# Revit family: Ghent - Reliant Series - Display Collection
name_source: partatom
category: Furniture
units: mm (PartAtom-declared; Revit-internal decimal feet)

## family parameters
Always vertical = Yes
Cut with Voids When Loaded = No
OmniClass Number = 23.40.20.00
OmniClass Title = General Furniture and Specialties
Room Calculation Point = No
Shared = No
Work Plane-Based = No

## types (7) — shared parameters
12 Shelves = No
Manufacturer = Ghent
Shelf Base Height = 1' - 0 3/8"
Side A Bottom = 1' - 9 1/2"
Side A Top = 1' - 0"
Side B Bottom = 0' - 9 1/2"
Side B Top = 2' - 1"
URL = https://ghent.com

## per-type parameters (varying)
| type | Case Height Interior | Cornice | Depth | Frame Height | Height | Model | Number of Shelves | Shelf Depth | Shelf Unit Width | Width |
| Floor Case with Vinyl Base - 72”H x 48”W x 16”D | 4' - 11 5/8" | No | 1' - 4" | 6' - 0" | 6' - 0" | 2074XX-XX-XX | 2 | 1' - 2" | 1' - 11 3/4" | 4' - 0" |
| Floor Case with Vinyl Base - 72”H x 60”W x 16”D | 4' - 11 5/8" | No | 1' - 4" | 6' - 0" | 6' - 0" | 2075XX-XX-XX | 2 | 1' - 2" | 2' - 5 3/4" | 5' - 0" |
| Floor Case with Vinyl Base - 72”H x 72”W x 16”D | 4' - 11 5/8" | No | 1' - 4" | 6' - 0" | 6' - 0" | 2076XX-XX-XX | 2 | 1' - 2" | 2' - 11 3/4" | 6' - 0" |
| Lighted Floor Case with Vinyl Base - 80"H x 48”W x 16”D | 4' - 11 5/8" | Yes | 1' - 4" | 6' - 0" | 6' - 8" | 2174XX-XX-XX | 2 | 1' - 2" | 1' - 11 3/4" | 4' - 0" |
| Lighted Floor Case with Vinyl Base - 80"H x 60”W x 16”D | 4' - 11 5/8" | Yes | 1' - 4" | 6' - 0" | 6' - 8" | 2175XX-XX-XX | 2 | 1' - 2" | 2' - 5 3/4" | 5' - 0" |
| Lighted Floor Case with Vinyl Base - 80"H x 72”W x 16”D | 4' - 11 5/8" | Yes | 1' - 4" | 6' - 0" | 6' - 8" | 2176XX-XX-XX | 2 | 1' - 2" | 2' - 11 3/4" | 6' - 0" |
| Lighted Floor Case with Vinyl Base - 40"H x 36”W x 14”D | 2' - 3 5/8" | No | 1' - 2" | 3' - 4" | 3' - 4" | 2281XX-XX-XX | 1 | 1' - 0" | 1' - 5 3/4" | 3' - 0" |

## geometry (parser evidence)
native form markers: Sweep x17
no freeform markers — native parametric forms only
